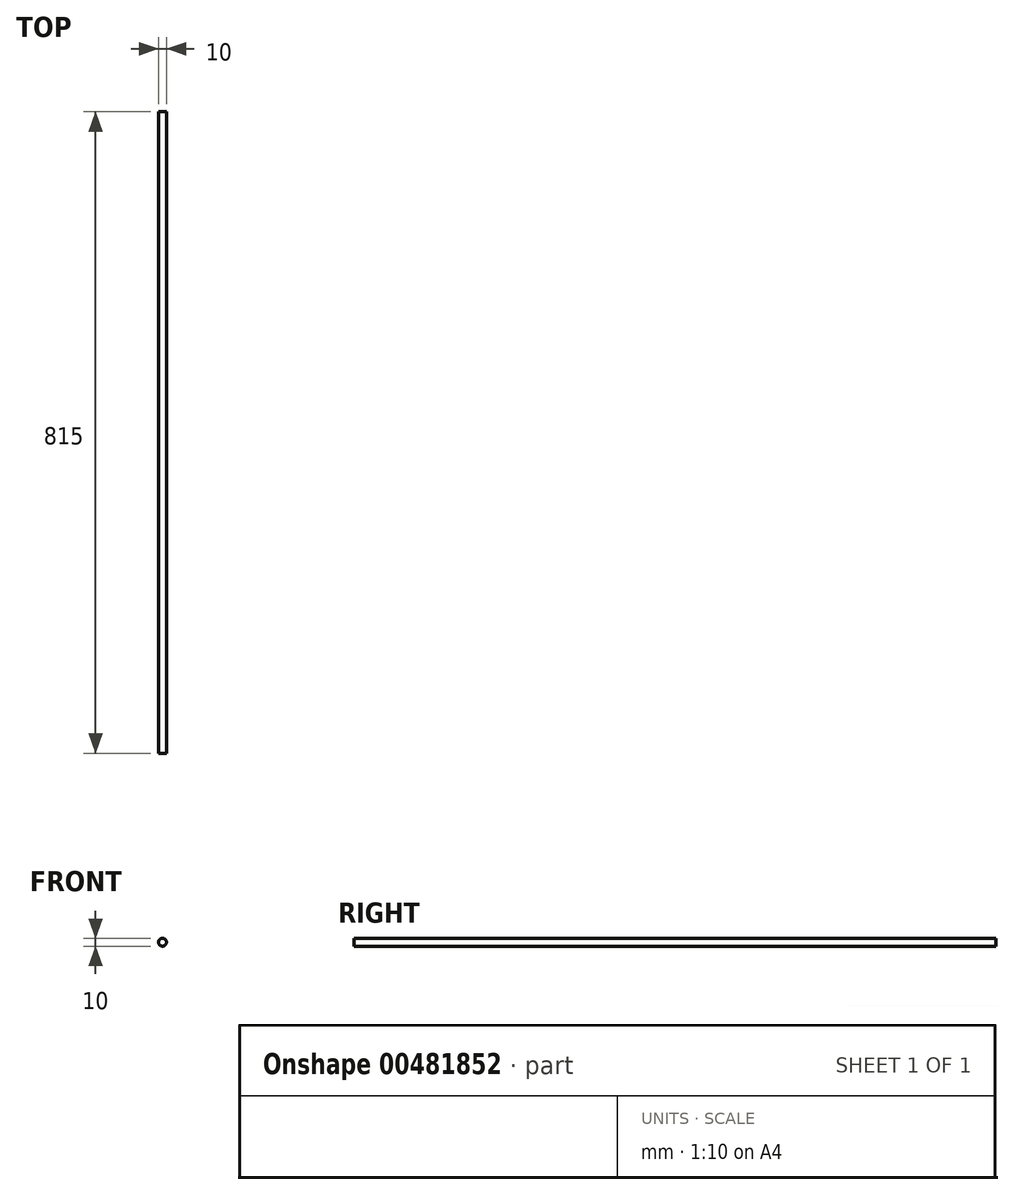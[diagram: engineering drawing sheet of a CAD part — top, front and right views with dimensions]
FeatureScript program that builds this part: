
annotation { "Feature Type Name" : "Feature", "Feature Type Description" : "" }
export const myFeature = defineFeature(function(context is Context, id is Id, definition is map)
    precondition{}
    {
        {
            var Q0;
            Q0=qCreatedBy(makeId("Front.planeOp"),FACE);
            var sketch = newSketch(context, id + "F0", { "sketchPlane" : qUnion([Q0])});
            skCircle(sketch, "E0", {"center": v(-55.36, 47.09) * mm, "radius": 5 * mm});
            skSolve(sketch);
        }
        {
            var Q0;
            Q0=makeQuery(id+"F0.imprint","IMPRINT",FACE,{"disambiguationData":[TD([[makeQuery(id+"F0.imprint","IMPRINT",EDGE,{"derivedFrom":sQuery(id+"F0.wireOp",EDGE,"E0")}),1.0]])]});
            extrude(context, id + "F1", {"entities" : qUnion([Q0]), "depth" : 815 * mm});
        }
    });
